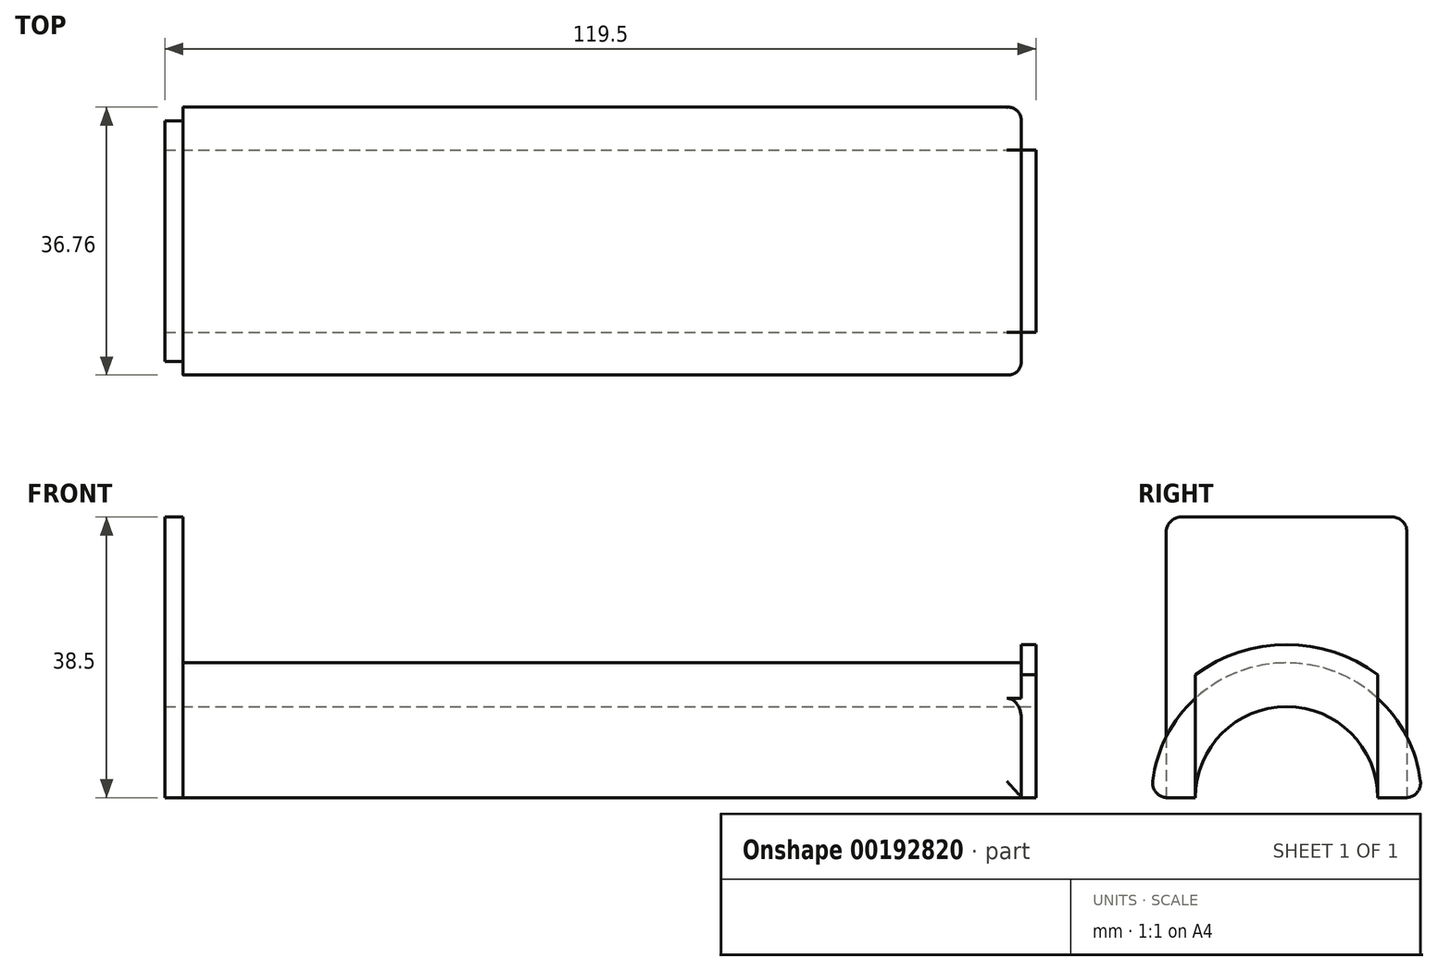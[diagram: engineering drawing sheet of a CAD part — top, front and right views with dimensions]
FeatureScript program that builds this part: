
annotation { "Feature Type Name" : "Feature", "Feature Type Description" : "" }
export const myFeature = defineFeature(function(context is Context, id is Id, definition is map)
    precondition{}
    {
        {
            var Q0;
            Q0=qCreatedBy(makeId("Right.planeOp"),FACE);
            var sketch = newSketch(context, id + "F0", { "sketchPlane" : qUnion([Q0])});
            skArc(sketch, "E0", {"start": v(18.5, 0) * mm, "mid": v(0, 18.5) * mm, "end": v(-18.5, 0) * mm});
            skLineSegment(sketch, "E1", {"start": v(-18.5, 0) * mm, "end": v(18.5, 0) * mm});
            skSolve(sketch);
        }
        {
            var Q0;
            Q0=makeQuery(id+"F0.imprint","IMPRINT",FACE,{"disambiguationData":[TD([[makeQuery(id+"F0.imprint","IMPRINT",EDGE,{"derivedFrom":sQuery(id+"F0.wireOp",EDGE,"E0")}),1.0]])]});
            extrude(context, id + "F1", {"entities" : qUnion([Q0]), "oppositeDirection" : true, "depth" : 115 * mm});
        }
        {
            var Q0;
            Q0=makeQuery(id+"F1.opExtrude","CAP_FACE",FACE,{"disambiguationData":[OSD([sQuery(id+"F0.wireOp",EDGE,"E0"),sQuery(id+"F0.wireOp",EDGE,"E1")])],"isStart":true});
            var sketch = newSketch(context, id + "F2", { "sketchPlane" : qUnion([Q0])});
            skLineSegment(sketch, "E2.bottom", {"start": v(-12.5, 21) * mm, "end": v(12.5, 21) * mm});
            skLineSegment(sketch, "E2.left", {"start": v(-12.5, 21) * mm, "end": v(-12.5, 0) * mm});
            skLineSegment(sketch, "E2.right", {"start": v(12.5, 21) * mm, "end": v(12.5, 0) * mm});
            skPoint(sketch, "E2.middle", {"position": v(0, 0) * mm});
            skLineSegment(sketch, "E3", {"start": v(-12.5, 0) * mm, "end": v(12.5, 0) * mm});
            skPoint(sketch, "E2.top.start.orphan", {"position": v(-12.5, -21) * mm});
            skPoint(sketch, "E4.orphan", {"position": v(12.5, -21) * mm});
            skSolve(sketch);
        }
        {
            var Q0;
            {var subQ0=sQuery(id+"F2.wireOp",EDGE,"E2.bottom");Q0=makeQuery(id+"F2.imprint","IMPRINT",FACE,{"disambiguationData":[TD([[makeQuery(id+"F2.imprint","IMPRINT",EDGE,{"derivedFrom":subQ0}),-1.0]])]});}
            var Q1;
            {var subQ0=sQuery(id+"F2.wireOp",EDGE,"E3");Q1=makeQuery(id+"F2.imprint","IMPRINT",FACE,{"disambiguationData":[TD([[makeQuery(id+"F2.imprint","IMPRINT",EDGE,{"derivedFrom":subQ0}),1.0]])]});}
            extrude(context, id + "F3", {"entities" : qUnion([Q0, Q1]), "operationType" : NewBodyOperationType.ADD, "depth" : 2 * mm});
        }
        {
            var Q0;
            Q0=makeQuery(id+"F1.opExtrude","CAP_FACE",FACE,{"disambiguationData":[OSD([sQuery(id+"F0.wireOp",EDGE,"E0"),sQuery(id+"F0.wireOp",EDGE,"E1")])],"isStart":false});
            var sketch = newSketch(context, id + "F4", { "sketchPlane" : qUnion([Q0])});
            skLineSegment(sketch, "E5", {"start": v(-18.5, 0) * mm, "end": v(18.5, 0) * mm});
            skLineSegment(sketch, "E6.bottom", {"start": v(16.5, 38.5) * mm, "end": v(-16.5, 38.5) * mm});
            skLineSegment(sketch, "E6.left", {"start": v(16.5, 38.5) * mm, "end": v(16.5, 0) * mm});
            skLineSegment(sketch, "E6.right", {"start": v(-16.5, 38.5) * mm, "end": v(-16.5, 0) * mm});
            skPoint(sketch, "E6.middle", {"position": v(0, 0) * mm});
            skPoint(sketch, "E6.top.end.orphan", {"position": v(-16.5, -38.5) * mm});
            skPoint(sketch, "E7.orphan", {"position": v(16.5, -38.5) * mm});
            skSolve(sketch);
        }
        {
            var Q0;
            {var subQ0=sQuery(id+"F4.wireOp",EDGE,"E6.left");var subQ1=sQuery(id+"F4.wireOp",EDGE,"E5");var subQ2=makeQuery(id+"F4.imprint","INTERSECT",VERTEX,{"derivedFrom":[subQ1,subQ0]});Q0=makeQuery(id+"F4.imprint","IMPRINT",FACE,{"disambiguationData":[TD([[makeQuery(id+"F4.imprint","IMPRINT",EDGE,{"disambiguationData":[TD([[subQ2,-1.0]])],"derivedFrom":subQ1}),-1.0]])]});}
            var Q1;
            {var subQ0=sQuery(id+"F4.wireOp",EDGE,"E6.bottom");Q1=makeQuery(id+"F4.imprint","IMPRINT",FACE,{"disambiguationData":[TD([[makeQuery(id+"F4.imprint","IMPRINT",EDGE,{"derivedFrom":subQ0}),1.0]])]});}
            extrude(context, id + "F5", {"entities" : qUnion([Q0, Q1]), "operationType" : NewBodyOperationType.ADD, "depth" : 2.5 * mm});
        }
        {
            var Q0;
            Q0=makeQuery(id+"F5.opExtrude","SWEPT_EDGE",EDGE,{"disambiguationData":[OSD([sQuery(id+"F4.wireOp",EDGE,"E6.bottom"),sQuery(id+"F4.wireOp",EDGE,"E6.right")])]});
            var Q1;
            Q1=makeQuery(id+"F5.opExtrude","SWEPT_EDGE",EDGE,{"disambiguationData":[OSD([sQuery(id+"F4.wireOp",EDGE,"E6.bottom"),sQuery(id+"F4.wireOp",EDGE,"E6.left")])]});
            fillet(context, id + "F6", {"entities" : qUnion([Q0, Q1]), "radius" : 2 * mm, "tangentPropagation" : true, "allowEdgeOverflow" : false});
        }
        {
            var Q0;
            Q0=makeQuery(id+"F3.opExtrude","CAP_FACE",FACE,{"disambiguationData":[OSD([sQuery(id+"F2.wireOp",EDGE,"E2.bottom"),sQuery(id+"F2.wireOp",EDGE,"E2.left"),sQuery(id+"F2.wireOp",EDGE,"E2.right"),sQuery(id+"F2.wireOp",EDGE,"E3")])],"isStart":false});
            var sketch = newSketch(context, id + "F7", { "sketchPlane" : qUnion([Q0])});
            skCircle(sketch, "E8", {"center": v(0, 0) * mm, "radius": 21 * mm});
            skSolve(sketch);
        }
        {
            var Q0;
            {var subQ0=sQuery(id+"F7.wireOp",EDGE,"E8");var subQ1=makeQuery(id+"F3.opExtrude","CAP_EDGE",EDGE,{"disambiguationData":[OSD([sQuery(id+"F2.wireOp",EDGE,"E2.bottom")])],"isStart":false});var subQ2=makeQuery(id+"F7.imprint","INTERSECT",VERTEX,{"derivedFrom":[subQ1,subQ0]});Q0=makeQuery(id+"F7.imprint","IMPRINT",FACE,{"disambiguationData":[TD([[makeQuery(id+"F7.imprint","IMPRINT",EDGE,{"disambiguationData":[TD([[subQ2,-1.0]])],"derivedFrom":subQ0}),-1.0]])]});}
            var Q1;
            {var subQ0=sQuery(id+"F7.wireOp",EDGE,"E8");var subQ1=makeQuery(id+"F3.opExtrude","CAP_EDGE",EDGE,{"disambiguationData":[OSD([sQuery(id+"F2.wireOp",EDGE,"E2.bottom")])],"isStart":false});var subQ2=makeQuery(id+"F7.imprint","INTERSECT",VERTEX,{"derivedFrom":[subQ1,subQ0]});Q1=makeQuery(id+"F7.imprint","IMPRINT",FACE,{"disambiguationData":[TD([[makeQuery(id+"F7.imprint","IMPRINT",EDGE,{"disambiguationData":[TD([[subQ2,1.0]])],"derivedFrom":subQ0}),-1.0]])]});}
            extrude(context, id + "F8", {"entities" : qUnion([Q0, Q1]), "operationType" : NewBodyOperationType.REMOVE, "oppositeDirection" : true, "depth" : 5 * mm});
        }
        {
            var Q0;
            Q0=makeQuery(id+"F3.opExtrude","CAP_FACE",FACE,{"disambiguationData":[OSD([sQuery(id+"F2.wireOp",EDGE,"E2.bottom"),sQuery(id+"F2.wireOp",EDGE,"E2.left"),sQuery(id+"F2.wireOp",EDGE,"E2.right"),sQuery(id+"F2.wireOp",EDGE,"E3")])],"isStart":false});
            var sketch = newSketch(context, id + "F9", { "sketchPlane" : qUnion([Q0])});
            skCircle(sketch, "E9", {"center": v(0, 0) * mm, "radius": 12.5 * mm});
            skSolve(sketch);
        }
        {
            var Q0;
            {var subQ1=makeQuery(id+"F3.opExtrude","CAP_EDGE",EDGE,{"disambiguationData":[OSD([sQuery(id+"F2.wireOp",EDGE,"E3")])],"isStart":false});Q0=makeQuery(id+"F9.imprint","IMPRINT",FACE,{"disambiguationData":[TD([[makeQuery(id+"F9.imprint","IMPRINT",EDGE,{"derivedFrom":subQ1}),1.0]])]});}
            extrude(context, id + "F10", {"entities" : qUnion([Q0]), "operationType" : NewBodyOperationType.REMOVE, "endBound" : BoundingType.UP_TO_NEXT, "oppositeDirection" : true, "depth" : 25 * mm});
        }
        {
            var Q0;
            {var subQ0=sQuery(id+"F2.wireOp",EDGE,"E3");var subQ1=sQuery(id+"F2.wireOp",EDGE,"E2.left");var subQ2=sQuery(id+"F0.wireOp",EDGE,"E1");var subQ3=sQuery(id+"F0.wireOp",EDGE,"E0");Q0=makeQuery(id+"F3.boolean.opBoolean","SPLIT",EDGE,{"disambiguationData":[TD([makeQuery(id+"F1.opExtrude","SWEPT_FACE",FACE,{"disambiguationData":[OSD([subQ3])]}),makeQuery(id+"F1.opExtrude","CAP_FACE",FACE,{"disambiguationData":[OSD([subQ3,subQ2])],"isStart":true}),makeQuery(id+"F1.opExtrude","SWEPT_FACE",FACE,{"disambiguationData":[OSD([subQ2])]}),makeQuery(id+"F3.opExtrude","CAP_FACE",FACE,{"disambiguationData":[OSD([sQuery(id+"F2.wireOp",EDGE,"E2.bottom"),subQ1,sQuery(id+"F2.wireOp",EDGE,"E2.right"),subQ0])],"isStart":true}),makeQuery(id+"F3.opExtrude","SWEPT_FACE",FACE,{"disambiguationData":[OSD([subQ1])]}),makeQuery(id+"F3.opExtrude","SWEPT_FACE",FACE,{"disambiguationData":[OSD([subQ0])]})])],"derivedFrom":makeQuery(id+"F1.opExtrude","CAP_EDGE",EDGE,{"disambiguationData":[OSD([subQ3])],"isStart":true})});}
            var Q1;
            {var subQ0=sQuery(id+"F0.wireOp",EDGE,"E1");var subQ1=sQuery(id+"F0.wireOp",EDGE,"E0");Q1=makeQuery(id+"F1.opExtrude","SWEPT_EDGE",EDGE,{"disambiguationData":[OSD([subQ1,subQ0]),TDD([makeQuery(id+"F0.imprint","INTERSECT",VERTEX,{"disambiguationData":[OD(1.0)],"derivedFrom":[subQ1,subQ0]})])]});}
            fillet(context, id + "F11", {"entities" : qUnion([Q0, Q1]), "radius" : 2 * mm, "tangentPropagation" : true, "allowEdgeOverflow" : false});
        }
        {
            var Q0;
            {var subQ0=sQuery(id+"F2.wireOp",EDGE,"E3");var subQ1=sQuery(id+"F2.wireOp",EDGE,"E2.right");var subQ2=sQuery(id+"F0.wireOp",EDGE,"E1");var subQ3=sQuery(id+"F0.wireOp",EDGE,"E0");Q0=makeQuery(id+"F3.boolean.opBoolean","SPLIT",EDGE,{"disambiguationData":[TD([makeQuery(id+"F1.opExtrude","SWEPT_FACE",FACE,{"disambiguationData":[OSD([subQ3])]}),makeQuery(id+"F1.opExtrude","CAP_FACE",FACE,{"disambiguationData":[OSD([subQ3,subQ2])],"isStart":true}),makeQuery(id+"F1.opExtrude","SWEPT_FACE",FACE,{"disambiguationData":[OSD([subQ2])]}),makeQuery(id+"F3.opExtrude","CAP_FACE",FACE,{"disambiguationData":[OSD([sQuery(id+"F2.wireOp",EDGE,"E2.bottom"),sQuery(id+"F2.wireOp",EDGE,"E2.left"),subQ1,subQ0])],"isStart":true}),makeQuery(id+"F3.opExtrude","SWEPT_FACE",FACE,{"disambiguationData":[OSD([subQ1])]}),makeQuery(id+"F3.opExtrude","SWEPT_FACE",FACE,{"disambiguationData":[OSD([subQ0])]})])],"derivedFrom":makeQuery(id+"F1.opExtrude","CAP_EDGE",EDGE,{"disambiguationData":[OSD([subQ3])],"isStart":true})});}
            var Q1;
            {var subQ0=sQuery(id+"F0.wireOp",EDGE,"E1");var subQ1=sQuery(id+"F0.wireOp",EDGE,"E0");Q1=makeQuery(id+"F1.opExtrude","SWEPT_EDGE",EDGE,{"disambiguationData":[OSD([subQ1,subQ0]),TDD([makeQuery(id+"F0.imprint","INTERSECT",VERTEX,{"disambiguationData":[OD(0.0)],"derivedFrom":[subQ1,subQ0]})])]});}
            fillet(context, id + "F12", {"entities" : qUnion([Q0, Q1]), "radius" : 2 * mm, "tangentPropagation" : true, "allowEdgeOverflow" : false});
        }
    });
